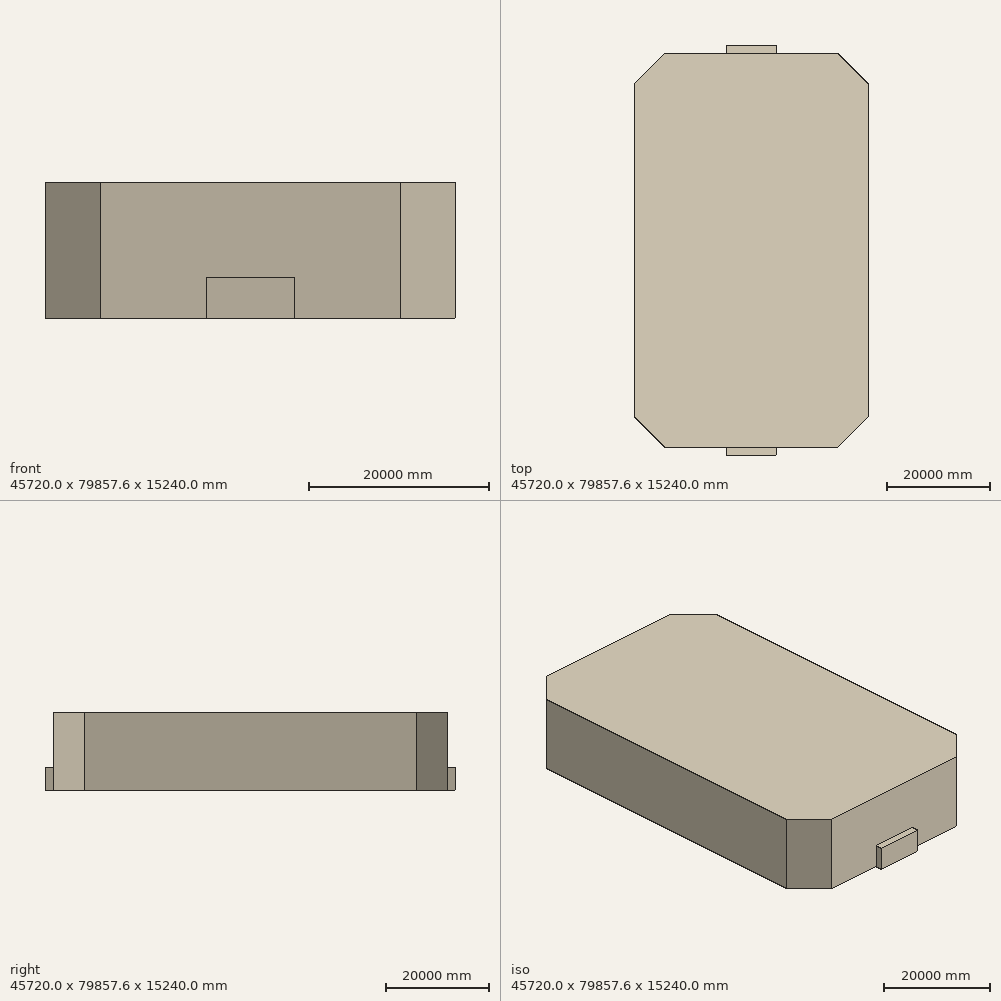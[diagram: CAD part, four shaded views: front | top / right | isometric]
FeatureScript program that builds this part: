
annotation { "Feature Type Name" : "Feature", "Feature Type Description" : "" }
export const myFeature = defineFeature(function(context is Context, id is Id, definition is map)
    precondition{}
    {
        {
            var Q0;
            Q0=qCreatedBy(makeId("Top.planeOp"),FACE);
            var sketch = newSketch(context, id + "F0", { "sketchPlane" : qUnion([Q0])});
            skLineSegment(sketch, "E0.bottom", {"start": v(22860, 38404.8) * mm, "end": v(-22860, 38404.8) * mm});
            skLineSegment(sketch, "E0.top", {"start": v(22860, -38404.8) * mm, "end": v(-22860, -38404.8) * mm});
            skLineSegment(sketch, "E0.left", {"start": v(22860, 38404.8) * mm, "end": v(22860, -38404.8) * mm});
            skLineSegment(sketch, "E0.right", {"start": v(-22860, 38404.8) * mm, "end": v(-22860, -38404.8) * mm});
            skPoint(sketch, "E0.middle", {"position": v(0, 0) * mm});
            skSolve(sketch);
        }
        {
            var Q0;
            Q0 = qSketchRegion(id + "F0", true);
            extrude(context, id + "F1", {"entities" : qUnion([Q0]), "depth" : 15240 * mm, "offsetDistance" : 25.4 * mm});
        }
        {
            var Q0;
            Q0=makeQuery(id+"F1.opExtrude","SWEPT_EDGE",EDGE,{"disambiguationData":[OSD([sQuery(id+"F0.wireOp",EDGE,"E0.top"),sQuery(id+"F0.wireOp",EDGE,"E0.left")])]});
            chamfer(context, id + "F2", {"entities" : qUnion([Q0]), "width" : 6096 * mm, "tangentPropagation" : true});
        }
        {
            var Q0;
            Q0=makeQuery(id+"F1.opExtrude","SWEPT_EDGE",EDGE,{"disambiguationData":[OSD([sQuery(id+"F0.wireOp",EDGE,"E0.top"),sQuery(id+"F0.wireOp",EDGE,"E0.right")])]});
            chamfer(context, id + "F3", {"entities" : qUnion([Q0]), "width" : 6096 * mm, "tangentPropagation" : true});
        }
        {
            var Q0;
            Q0=makeQuery(id+"F1.opExtrude","SWEPT_EDGE",EDGE,{"disambiguationData":[OSD([sQuery(id+"F0.wireOp",EDGE,"E0.bottom"),sQuery(id+"F0.wireOp",EDGE,"E0.left")])]});
            var Q1;
            Q1=makeQuery(id+"F1.opExtrude","SWEPT_EDGE",EDGE,{"disambiguationData":[OSD([sQuery(id+"F0.wireOp",EDGE,"E0.bottom"),sQuery(id+"F0.wireOp",EDGE,"E0.right")])]});
            chamfer(context, id + "F4", {"entities" : qUnion([Q0, Q1]), "width" : 6096 * mm, "tangentPropagation" : true});
        }
        {
            var Q0;
            Q0=makeQuery(id+"F1.opExtrude","SWEPT_FACE",FACE,{"disambiguationData":[OSD([sQuery(id+"F0.wireOp",EDGE,"E0.bottom")])]});
            var sketch = newSketch(context, id + "F5", { "sketchPlane" : qUnion([Q0])});
            skLineSegment(sketch, "E1.bottom", {"start": v(0, 4572) * mm, "end": v(4876.8, 4572) * mm});
            skLineSegment(sketch, "E1.top", {"start": v(0, 0) * mm, "end": v(4876.8, 0) * mm});
            skLineSegment(sketch, "E1.left", {"start": v(0, 4572) * mm, "end": v(0, 0) * mm});
            skLineSegment(sketch, "E1.right", {"start": v(4876.8, 4572) * mm, "end": v(4876.8, 0) * mm});
            skLineSegment(sketch, "E2.bottom", {"start": v(0, 4572) * mm, "end": v(-4876.8, 4572) * mm});
            skLineSegment(sketch, "E2.top", {"start": v(0, 0) * mm, "end": v(-4876.8, 0) * mm});
            skLineSegment(sketch, "E2.right", {"start": v(-4876.8, 4572) * mm, "end": v(-4876.8, 0) * mm});
            skSolve(sketch);
        }
        {
            var Q0;
            Q0 = qSketchRegion(id + "F5", true);
            extrude(context, id + "F6", {"entities" : qUnion([Q0]), "operationType" : NewBodyOperationType.ADD, "depth" : 1524 * mm, "offsetDistance" : 25.4 * mm});
        }
        {
            var Q0;
            Q0=makeQuery(id+"F1.opExtrude","SWEPT_FACE",FACE,{"disambiguationData":[OSD([sQuery(id+"F0.wireOp",EDGE,"E0.top")])]});
            var sketch = newSketch(context, id + "F7", { "sketchPlane" : qUnion([Q0])});
            skLineSegment(sketch, "E3.bottom", {"start": v(0, 4572) * mm, "end": v(4876.8, 4572) * mm});
            skLineSegment(sketch, "E3.top", {"start": v(0, 0) * mm, "end": v(4876.8, 0) * mm});
            skLineSegment(sketch, "E3.left", {"start": v(0, 4572) * mm, "end": v(0, 0) * mm});
            skLineSegment(sketch, "E3.right", {"start": v(4876.8, 4572) * mm, "end": v(4876.8, 0) * mm});
            skLineSegment(sketch, "E4.bottom", {"start": v(0, 4572) * mm, "end": v(-4876.8, 4572) * mm});
            skLineSegment(sketch, "E4.top", {"start": v(0, 0) * mm, "end": v(-4876.8, 0) * mm});
            skLineSegment(sketch, "E4.right", {"start": v(-4876.8, 4572) * mm, "end": v(-4876.8, 0) * mm});
            skSolve(sketch);
        }
        {
            var Q0;
            Q0 = qSketchRegion(id + "F7", true);
            extrude(context, id + "F8", {"entities" : qUnion([Q0]), "operationType" : NewBodyOperationType.ADD, "depth" : 1524 * mm, "offsetDistance" : 25.4 * mm});
        }
    });
